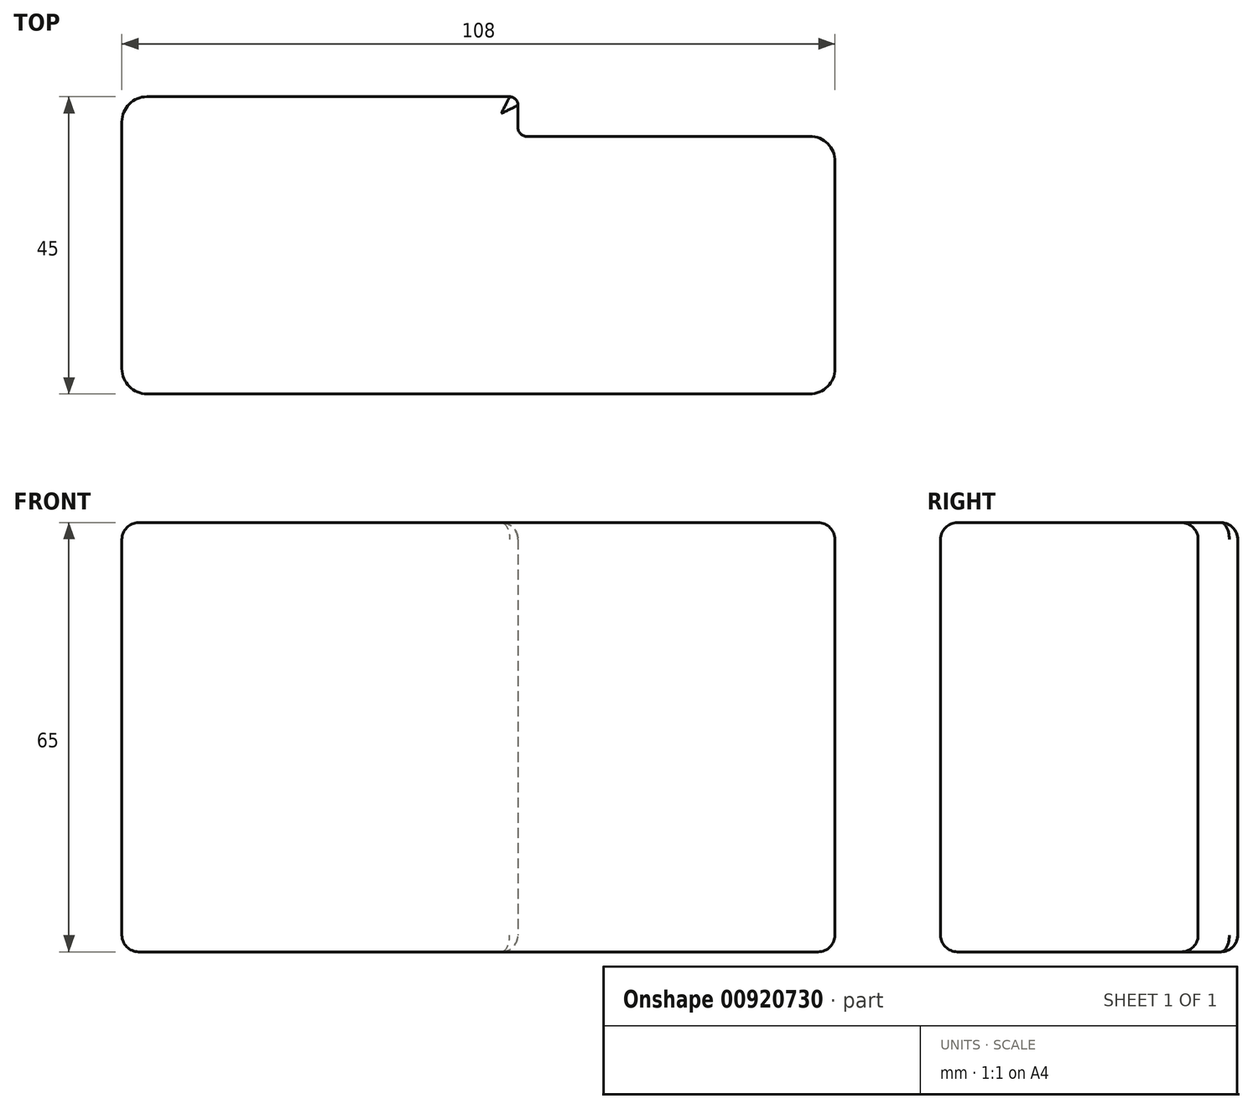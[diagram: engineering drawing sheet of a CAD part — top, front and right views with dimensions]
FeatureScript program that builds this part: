
annotation { "Feature Type Name" : "Feature", "Feature Type Description" : "" }
export const myFeature = defineFeature(function(context is Context, id is Id, definition is map)
    precondition{}
    {
        {
            var Q0;
            Q0=qCreatedBy(makeId("Top.planeOp"),FACE);
            var sketch = newSketch(context, id + "F0", { "sketchPlane" : qUnion([Q0])});
            skLineSegment(sketch, "E0", {"start": v(-44.45, 19.26) * mm, "end": v(-44.45, -18.12) * mm});
            skLineSegment(sketch, "E1", {"start": v(-40.64, -21.93) * mm, "end": v(59.74, -21.93) * mm});
            skLineSegment(sketch, "E2", {"start": v(63.55, -18.12) * mm, "end": v(63.55, 13.26) * mm});
            skLineSegment(sketch, "E3", {"start": v(59.74, 17.07) * mm, "end": v(16.82, 17.07) * mm});
            skLineSegment(sketch, "E4", {"start": v(15.55, 18.34) * mm, "end": v(15.55, 21.8) * mm});
            skLineSegment(sketch, "E5", {"start": v(14.28, 23.07) * mm, "end": v(-40.64, 23.07) * mm});
            skPoint(sketch, "E6.visualSharp", {"position": v(-44.45, 23.07) * mm});
            skArc(sketch, "E6.filletArc", {"start": v(-40.64, 23.07) * mm, "mid": v(-43.34, 21.95) * mm, "end": v(-44.45, 19.26) * mm});
            skPoint(sketch, "E7.visualSharp", {"position": v(-44.45, -21.93) * mm});
            skArc(sketch, "E7.filletArc", {"start": v(-44.45, -18.12) * mm, "mid": v(-43.34, -20.82) * mm, "end": v(-40.64, -21.93) * mm});
            skPoint(sketch, "E8.visualSharp", {"position": v(63.55, -21.93) * mm});
            skArc(sketch, "E8.filletArc", {"start": v(59.74, -21.93) * mm, "mid": v(62.43, -20.82) * mm, "end": v(63.55, -18.12) * mm});
            skPoint(sketch, "E9.visualSharp", {"position": v(63.55, 17.07) * mm});
            skArc(sketch, "E9.filletArc", {"start": v(63.55, 13.26) * mm, "mid": v(62.43, 15.95) * mm, "end": v(59.74, 17.07) * mm});
            skPoint(sketch, "E10.visualSharp", {"position": v(15.55, 23.07) * mm});
            skArc(sketch, "E10.filletArc", {"start": v(15.55, 21.8) * mm, "mid": v(15.18, 22.7) * mm, "end": v(14.28, 23.07) * mm});
            skPoint(sketch, "E11.visualSharp", {"position": v(15.55, 17.07) * mm});
            skArc(sketch, "E11.filletArc", {"start": v(15.55, 18.34) * mm, "mid": v(15.92, 17.44) * mm, "end": v(16.82, 17.07) * mm});
            skSolve(sketch);
        }
        {
            var Q0;
            Q0=makeQuery(id+"F0.imprint","IMPRINT",FACE,{"disambiguationData":[TD([[makeQuery(id+"F0.imprint","IMPRINT",EDGE,{"derivedFrom":sQuery(id+"F0.wireOp",EDGE,"E0")}),1.0]])]});
            extrude(context, id + "F1", {"entities" : qUnion([Q0]), "depth" : 65 * mm, "offsetDistance" : 25.4 * mm});
        }
        {
            var Q0;
            Q0=makeQuery(id+"F1.opExtrude","CAP_FACE",FACE,{"disambiguationData":[OSD([sQuery(id+"F0.wireOp",EDGE,"E0"),sQuery(id+"F0.wireOp",EDGE,"E1"),sQuery(id+"F0.wireOp",EDGE,"E2"),sQuery(id+"F0.wireOp",EDGE,"E3"),sQuery(id+"F0.wireOp",EDGE,"E4"),sQuery(id+"F0.wireOp",EDGE,"E5"),sQuery(id+"F0.wireOp",EDGE,"E6.filletArc"),sQuery(id+"F0.wireOp",EDGE,"E7.filletArc"),sQuery(id+"F0.wireOp",EDGE,"E8.filletArc"),sQuery(id+"F0.wireOp",EDGE,"E9.filletArc"),sQuery(id+"F0.wireOp",EDGE,"E10.filletArc"),sQuery(id+"F0.wireOp",EDGE,"E11.filletArc")])],"isStart":true});
            fillet(context, id + "F2", {"entities" : qUnion([Q0]), "radius" : 2.54 * mm, "tangentPropagation" : true, "allowEdgeOverflow" : false});
        }
        {
            var Q0;
            Q0=makeQuery(id+"F1.opExtrude","CAP_FACE",FACE,{"disambiguationData":[OSD([sQuery(id+"F0.wireOp",EDGE,"E0"),sQuery(id+"F0.wireOp",EDGE,"E1"),sQuery(id+"F0.wireOp",EDGE,"E2"),sQuery(id+"F0.wireOp",EDGE,"E3"),sQuery(id+"F0.wireOp",EDGE,"E4"),sQuery(id+"F0.wireOp",EDGE,"E5"),sQuery(id+"F0.wireOp",EDGE,"E6.filletArc"),sQuery(id+"F0.wireOp",EDGE,"E7.filletArc"),sQuery(id+"F0.wireOp",EDGE,"E8.filletArc"),sQuery(id+"F0.wireOp",EDGE,"E9.filletArc"),sQuery(id+"F0.wireOp",EDGE,"E10.filletArc"),sQuery(id+"F0.wireOp",EDGE,"E11.filletArc")])],"isStart":false});
            fillet(context, id + "F3", {"entities" : qUnion([Q0]), "radius" : 2.54 * mm, "tangentPropagation" : true, "allowEdgeOverflow" : false});
        }
        {
            var Q0;
            Q0=makeQuery(id+"F1.opExtrude","CAP_FACE",FACE,{"disambiguationData":[OSD([sQuery(id+"F0.wireOp",EDGE,"E0"),sQuery(id+"F0.wireOp",EDGE,"E1"),sQuery(id+"F0.wireOp",EDGE,"E2"),sQuery(id+"F0.wireOp",EDGE,"E3"),sQuery(id+"F0.wireOp",EDGE,"E4"),sQuery(id+"F0.wireOp",EDGE,"E5"),sQuery(id+"F0.wireOp",EDGE,"E6.filletArc"),sQuery(id+"F0.wireOp",EDGE,"E7.filletArc"),sQuery(id+"F0.wireOp",EDGE,"E8.filletArc"),sQuery(id+"F0.wireOp",EDGE,"E9.filletArc"),sQuery(id+"F0.wireOp",EDGE,"E10.filletArc"),sQuery(id+"F0.wireOp",EDGE,"E11.filletArc")])],"isStart":false});
            var sketch = newSketch(context, id + "F4", { "sketchPlane" : qUnion([Q0])});
            skLineSegment(sketch, "E12", {"start": v(-36.91, -14.4) * mm, "end": v(-25.41, -14.4) * mm});
            skLineSegment(sketch, "E13", {"start": v(-25.41, -14.4) * mm, "end": v(-25.41, -12.9) * mm});
            skLineSegment(sketch, "E14", {"start": v(-25.41, -12.9) * mm, "end": v(-36.91, -12.9) * mm});
            skLineSegment(sketch, "E15", {"start": v(-36.91, -12.9) * mm, "end": v(-36.91, -14.4) * mm});
            skLineSegment(sketch, "E16", {"start": v(-25.41, -14.4) * mm, "end": v(-18.2, -14.4) * mm});
            skLineSegment(sketch, "E17", {"start": v(-18.2, -14.4) * mm, "end": v(-18.2, -12.9) * mm});
            skLineSegment(sketch, "E18", {"start": v(-18.2, -12.9) * mm, "end": v(-25.41, -12.9) * mm});
            skLineSegment(sketch, "E19", {"start": v(-36.7, -5.65) * mm, "end": v(-25.9, -5.65) * mm});
            skLineSegment(sketch, "E20", {"start": v(-25.9, -5.65) * mm, "end": v(-25.9, -3.02) * mm});
            skLineSegment(sketch, "E21", {"start": v(-25.9, -3.02) * mm, "end": v(-36.7, -3.02) * mm});
            skLineSegment(sketch, "E22", {"start": v(-36.7, -3.02) * mm, "end": v(-36.7, -5.65) * mm});
            skLineSegment(sketch, "E23", {"start": v(-17.72, -5.65) * mm, "end": v(-17.72, -3.02) * mm});
            skLineSegment(sketch, "E24", {"start": v(-17.72, -3.02) * mm, "end": v(-25.9, -3.02) * mm});
            skLineSegment(sketch, "E25", {"start": v(-25.9, -5.65) * mm, "end": v(-17.72, -5.65) * mm});
            skSolve(sketch);
        }
        {
            var Q0;
            Q0=makeQuery(id+"F4.imprint","IMPRINT",FACE,{"disambiguationData":[TD([[makeQuery(id+"F4.imprint","IMPRINT",EDGE,{"derivedFrom":sQuery(id+"F4.wireOp",EDGE,"E12")}),1.0]])]});
            extrude(context, id + "F5", {"entities" : qUnion([Q0]), "operationType" : NewBodyOperationType.ADD, "oppositeDirection" : true, "depth" : 15.5 * mm, "offsetDistance" : 25.4 * mm});
        }
        {
            var Q0;
            Q0=makeQuery(id+"F4.imprint","IMPRINT",FACE,{"disambiguationData":[TD([[makeQuery(id+"F4.imprint","IMPRINT",EDGE,{"derivedFrom":sQuery(id+"F4.wireOp",EDGE,"E13")}),-1.0]])]});
            extrude(context, id + "F6", {"entities" : qUnion([Q0]), "operationType" : NewBodyOperationType.ADD, "oppositeDirection" : true, "depth" : 2.54 * mm, "offsetDistance" : 25.4 * mm});
        }
    });
